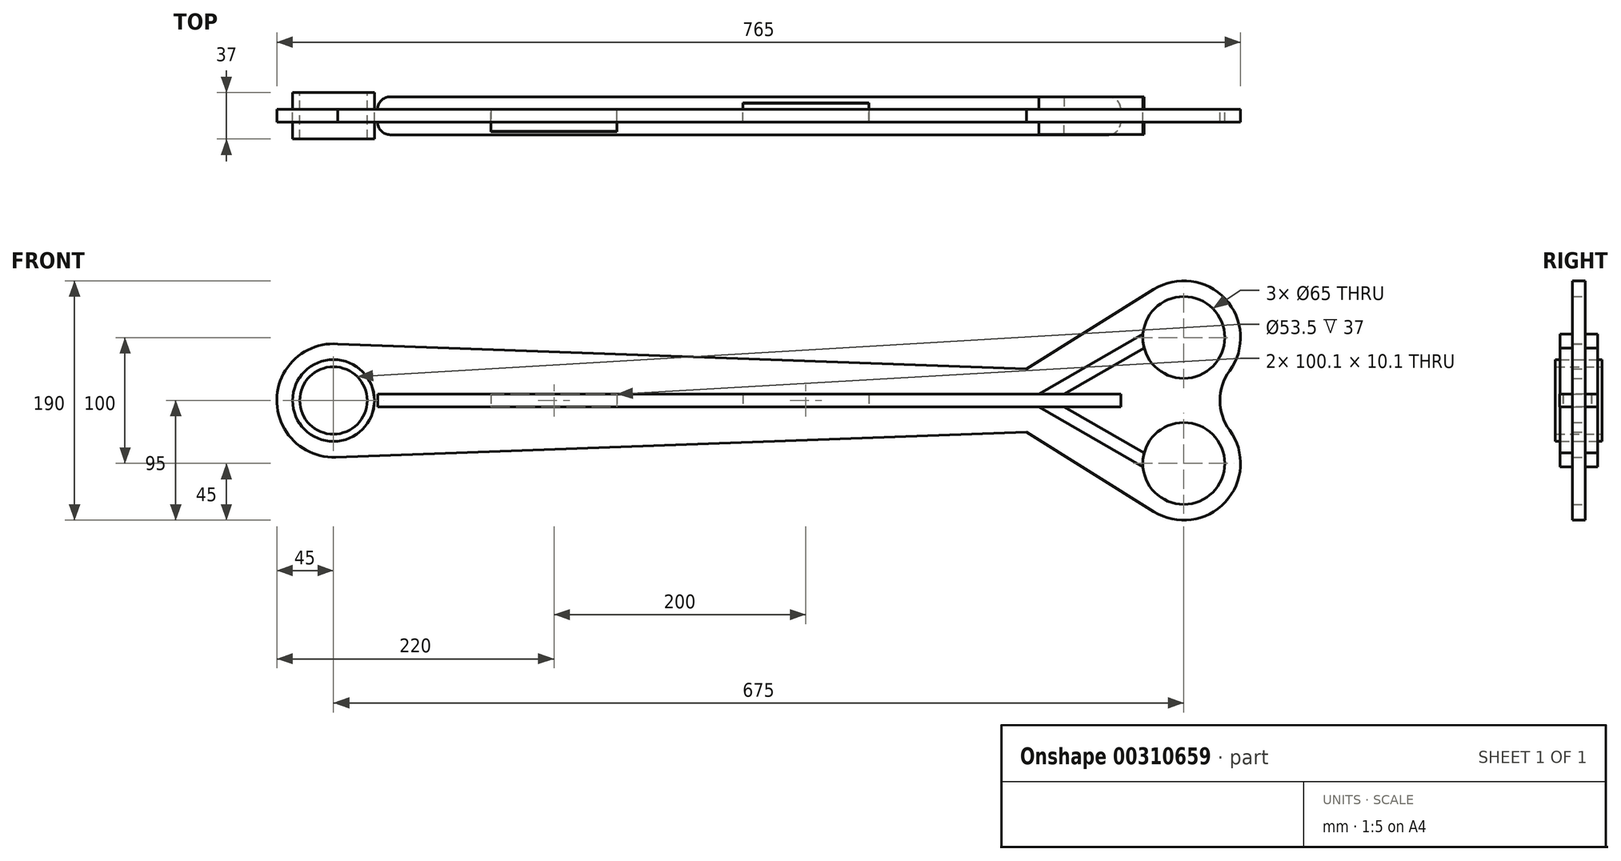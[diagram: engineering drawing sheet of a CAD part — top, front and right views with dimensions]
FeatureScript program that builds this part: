
annotation { "Feature Type Name" : "Feature", "Feature Type Description" : "" }
export const myFeature = defineFeature(function(context is Context, id is Id, definition is map)
    precondition{}
    {
        {
            var Q0;
            Q0=qCreatedBy(makeId("Front.planeOp"),FACE);
            var sketch = newSketch(context, id + "F0", { "sketchPlane" : qUnion([Q0])});
            skCircle(sketch, "E0", {"center": v(0, 0) * mm, "radius": 32.5 * mm});
            skCircle(sketch, "E1", {"center": v(0, 0) * mm, "radius": 45 * mm});
            skCircle(sketch, "E2", {"center": v(750, 0) * mm, "radius": 32.5 * mm, "construction": true});
            skCircle(sketch, "E3", {"center": v(675, 50) * mm, "radius": 32.5 * mm});
            skCircle(sketch, "E4", {"center": v(675, -50) * mm, "radius": 32.5 * mm});
            skCircle(sketch, "E5", {"center": v(675, 50) * mm, "radius": 45 * mm});
            skArc(sketch, "E6", {"start": v(651.17, -88.17) * mm, "mid": v(707.92, -80.68) * mm, "end": v(711.4, -23.53) * mm});
            skLineSegment(sketch, "E7", {"start": v(550, 25) * mm, "end": v(550, -25) * mm, "construction": true});
            skPoint(sketch, "E8", {"position": v(550, 0) * mm});
            skLineSegment(sketch, "E9", {"start": v(0, 45) * mm, "end": v(550, 25) * mm});
            skLineSegment(sketch, "E10", {"start": v(550, -25) * mm, "end": v(0, -45.03) * mm});
            skLineSegment(sketch, "E11", {"start": v(550, 25) * mm, "end": v(651.17, 88.17) * mm});
            skLineSegment(sketch, "E12", {"start": v(550, -25) * mm, "end": v(651.17, -88.17) * mm});
            skArc(sketch, "E13", {"start": v(711.4, 23.53) * mm, "mid": v(703.74, 0) * mm, "end": v(711.4, -23.53) * mm});
            skLineSegment(sketch, "E14.bottom", {"start": v(124.95, 5.05) * mm, "end": v(225.05, 5.05) * mm});
            skLineSegment(sketch, "E14.top", {"start": v(124.95, -5.05) * mm, "end": v(225.05, -5.05) * mm});
            skLineSegment(sketch, "E14.left", {"start": v(124.95, 5.05) * mm, "end": v(124.95, -5.05) * mm});
            skLineSegment(sketch, "E14.right", {"start": v(225.05, 5.05) * mm, "end": v(225.05, -5.05) * mm});
            skLineSegment(sketch, "E15.bottom", {"start": v(324.95, 5.05) * mm, "end": v(425.05, 5.05) * mm});
            skLineSegment(sketch, "E15.top", {"start": v(324.95, -5.05) * mm, "end": v(425.05, -5.05) * mm});
            skLineSegment(sketch, "E15.left", {"start": v(324.95, 5.05) * mm, "end": v(324.95, -5.05) * mm});
            skLineSegment(sketch, "E15.right", {"start": v(425.05, 5.05) * mm, "end": v(425.05, -5.05) * mm});
            skSolve(sketch);
        }
        {
            var Q0;
            Q0 = qSketchRegion(id + "F0", true);
            extrude(context, id + "F1", {"entities" : qUnion([Q0]), "depth" : 5 * mm, "hasSecondDirection" : true, "secondDirectionOppositeDirection" : true, "secondDirectionDepth" : 5 * mm});
        }
        {
            var Q0;
            Q0=qCreatedBy(makeId("Top.planeOp"),FACE);
            var sketch = newSketch(context, id + "F2", { "sketchPlane" : qUnion([Q0])});
            skLineSegment(sketch, "E16", {"start": v(35, 5.05) * mm, "end": v(35, 5.05) * mm});
            skLineSegment(sketch, "E17", {"start": v(45, 15.05) * mm, "end": v(615, 15.05) * mm});
            skLineSegment(sketch, "E18", {"start": v(35, 5.05) * mm, "end": v(324.9, 5.05) * mm});
            skLineSegment(sketch, "E19", {"start": v(625, 5.05) * mm, "end": v(625, 5.05) * mm});
            skLineSegment(sketch, "E20", {"start": v(125, 5.05) * mm, "end": v(125, -12.45) * mm});
            skLineSegment(sketch, "E21", {"start": v(125, -12.45) * mm, "end": v(225, -12.45) * mm});
            skLineSegment(sketch, "E22", {"start": v(225, -12.45) * mm, "end": v(225, 5.05) * mm});
            skLineSegment(sketch, "E23", {"start": v(324.9, 5.05) * mm, "end": v(324.9, 10.15) * mm});
            skLineSegment(sketch, "E24", {"start": v(324.9, 10.15) * mm, "end": v(425.1, 10.15) * mm});
            skLineSegment(sketch, "E25", {"start": v(425.1, 10.15) * mm, "end": v(425.1, 5.05) * mm});
            skLineSegment(sketch, "E26.trimOffspring", {"start": v(425.1, 5.05) * mm, "end": v(625, 5.05) * mm});
            skPoint(sketch, "E27.visualSharp", {"position": v(35, 15.05) * mm});
            skArc(sketch, "E27.filletArc", {"start": v(45, 15.05) * mm, "mid": v(37.93, 12.12) * mm, "end": v(35, 5.05) * mm});
            skPoint(sketch, "E28.visualSharp", {"position": v(625, 15.05) * mm});
            skArc(sketch, "E28.filletArc", {"start": v(625, 5.05) * mm, "mid": v(622.07, 12.12) * mm, "end": v(615, 15.05) * mm});
            skLineSegment(sketch, "E29", {"start": v(35, -5.05) * mm, "end": v(35, -5.05) * mm});
            skLineSegment(sketch, "E30", {"start": v(45, -15.05) * mm, "end": v(615, -15.05) * mm});
            skLineSegment(sketch, "E31", {"start": v(625, -5.05) * mm, "end": v(625, -5.05) * mm});
            skLineSegment(sketch, "E32", {"start": v(625, -5.05) * mm, "end": v(225.05, -5.05) * mm});
            skLineSegment(sketch, "E33", {"start": v(124.95, -5.05) * mm, "end": v(124.95, -12.55) * mm});
            skLineSegment(sketch, "E34", {"start": v(124.95, -12.55) * mm, "end": v(225.05, -12.55) * mm});
            skLineSegment(sketch, "E35", {"start": v(225.05, -12.55) * mm, "end": v(225.05, -5.05) * mm});
            skLineSegment(sketch, "E36.trimOffspring", {"start": v(124.95, -5.05) * mm, "end": v(35, -5.05) * mm});
            skLineSegment(sketch, "E37", {"start": v(325, -5.05) * mm, "end": v(325, 10.05) * mm});
            skLineSegment(sketch, "E38", {"start": v(325, 10.05) * mm, "end": v(425, 10.05) * mm});
            skLineSegment(sketch, "E39", {"start": v(425, 10.05) * mm, "end": v(425, -5.05) * mm});
            skPoint(sketch, "E40.visualSharp", {"position": v(625, -15.05) * mm});
            skArc(sketch, "E40.filletArc", {"start": v(615, -15.05) * mm, "mid": v(622.07, -12.12) * mm, "end": v(625, -5.05) * mm});
            skPoint(sketch, "E41.visualSharp", {"position": v(35, -15.05) * mm});
            skArc(sketch, "E41.filletArc", {"start": v(35, -5.05) * mm, "mid": v(37.93, -12.12) * mm, "end": v(45, -15.05) * mm});
            skSolve(sketch);
        }
        {
            var Q0;
            Q0 = qSketchRegion(id + "F2", true);
            extrude(context, id + "F3", {"entities" : qUnion([Q0]), "depth" : 5 * mm, "hasSecondDirection" : true, "secondDirectionOppositeDirection" : true, "secondDirectionDepth" : 5 * mm});
        }
        {
            var Q0;
            Q0=makeQuery(id+"F1.opExtrude","CAP_FACE",FACE,{"disambiguationData":[OSD([sQuery(id+"F0.wireOp",EDGE,"E0"),sQuery(id+"F0.wireOp",EDGE,"E1"),sQuery(id+"F0.wireOp",EDGE,"E3"),sQuery(id+"F0.wireOp",EDGE,"E4"),sQuery(id+"F0.wireOp",EDGE,"E5"),sQuery(id+"F0.wireOp",EDGE,"E6"),sQuery(id+"F0.wireOp",EDGE,"E9"),sQuery(id+"F0.wireOp",EDGE,"E10"),sQuery(id+"F0.wireOp",EDGE,"E11"),sQuery(id+"F0.wireOp",EDGE,"E12"),sQuery(id+"F0.wireOp",EDGE,"E13"),sQuery(id+"F0.wireOp",EDGE,"E14.bottom"),sQuery(id+"F0.wireOp",EDGE,"E14.top"),sQuery(id+"F0.wireOp",EDGE,"E14.left"),sQuery(id+"F0.wireOp",EDGE,"E14.right"),sQuery(id+"F0.wireOp",EDGE,"E15.bottom"),sQuery(id+"F0.wireOp",EDGE,"E15.top"),sQuery(id+"F0.wireOp",EDGE,"E15.left"),sQuery(id+"F0.wireOp",EDGE,"E15.right")])],"isStart":true});
            var sketch = newSketch(context, id + "F4", { "sketchPlane" : qUnion([Q0])});
            skLineSegment(sketch, "E42", {"start": v(-643.46, -41.74) * mm, "end": v(-580, -5.1) * mm});
            skLineSegment(sketch, "E43", {"start": v(-580, -5.1) * mm, "end": v(-560, -5.1) * mm});
            skLineSegment(sketch, "E44", {"start": v(-560, -5.1) * mm, "end": v(-642.52, -52.74) * mm});
            skCircle(sketch, "E45", {"center": v(-675, -50) * mm, "radius": 32.6 * mm, "construction": true});
            skArc(sketch, "E46", {"start": v(-642.52, -52.74) * mm, "mid": v(-642.52, -47.2) * mm, "end": v(-643.46, -41.74) * mm});
            skLineSegment(sketch, "E47.MirrorCS", {"start": v(-580, 5.1) * mm, "end": v(-560, 5.1) * mm});
            skArc(sketch, "E48.MirrorCS", {"start": v(-642.52, 52.74) * mm, "mid": v(-642.52, 47.2) * mm, "end": v(-643.46, 41.74) * mm});
            skLineSegment(sketch, "E49.MirrorCS", {"start": v(-643.46, 41.74) * mm, "end": v(-580, 5.1) * mm});
            skLineSegment(sketch, "E50.MirrorCS", {"start": v(-560, 5.1) * mm, "end": v(-642.52, 52.74) * mm});
            skSolve(sketch);
        }
        {
            var Q0;
            Q0 = qSketchRegion(id + "F4", true);
            extrude(context, id + "F5", {"entities" : qUnion([Q0]), "depth" : 10 * mm});
        }
        {
            var Q0;
            Q0=makeQuery(id+"F5.opExtrude","SWEPT_BODY",BODY,{"disambiguationData":[OSD([sQuery(id+"F4.wireOp",EDGE,"E47.MirrorCS"),sQuery(id+"F4.wireOp",EDGE,"E48.MirrorCS"),sQuery(id+"F4.wireOp",EDGE,"E49.MirrorCS"),sQuery(id+"F4.wireOp",EDGE,"E50.MirrorCS")])]});
            var Q1;
            Q1=makeQuery(id+"F5.opExtrude","SWEPT_BODY",BODY,{"disambiguationData":[OSD([sQuery(id+"F4.wireOp",EDGE,"E42"),sQuery(id+"F4.wireOp",EDGE,"E43"),sQuery(id+"F4.wireOp",EDGE,"E44"),sQuery(id+"F4.wireOp",EDGE,"E46")])]});
            var Q2;
            Q2=qCreatedBy(makeId("Front.planeOp"),FACE);
            mirror(context, id + "F6", {"entities" : qUnion([Q0, Q1]), "mirrorPlane" : qUnion([Q2])});
        }
        {
            var Q0;
            Q0=qCreatedBy(makeId("Front.planeOp"),FACE);
            var sketch = newSketch(context, id + "F7", { "sketchPlane" : qUnion([Q0])});
            skCircle(sketch, "E51", {"center": v(0, 0) * mm, "radius": 32.45 * mm});
            skCircle(sketch, "E52", {"center": v(0, 0) * mm, "radius": 26.75 * mm});
            skSolve(sketch);
        }
        {
            var Q0;
            Q0 = qSketchRegion(id + "F7", true);
            extrude(context, id + "F8", {"entities" : qUnion([Q0]), "depth" : 18.5 * mm, "hasSecondDirection" : true, "secondDirectionOppositeDirection" : true, "secondDirectionDepth" : 18.5 * mm});
        }
    });
